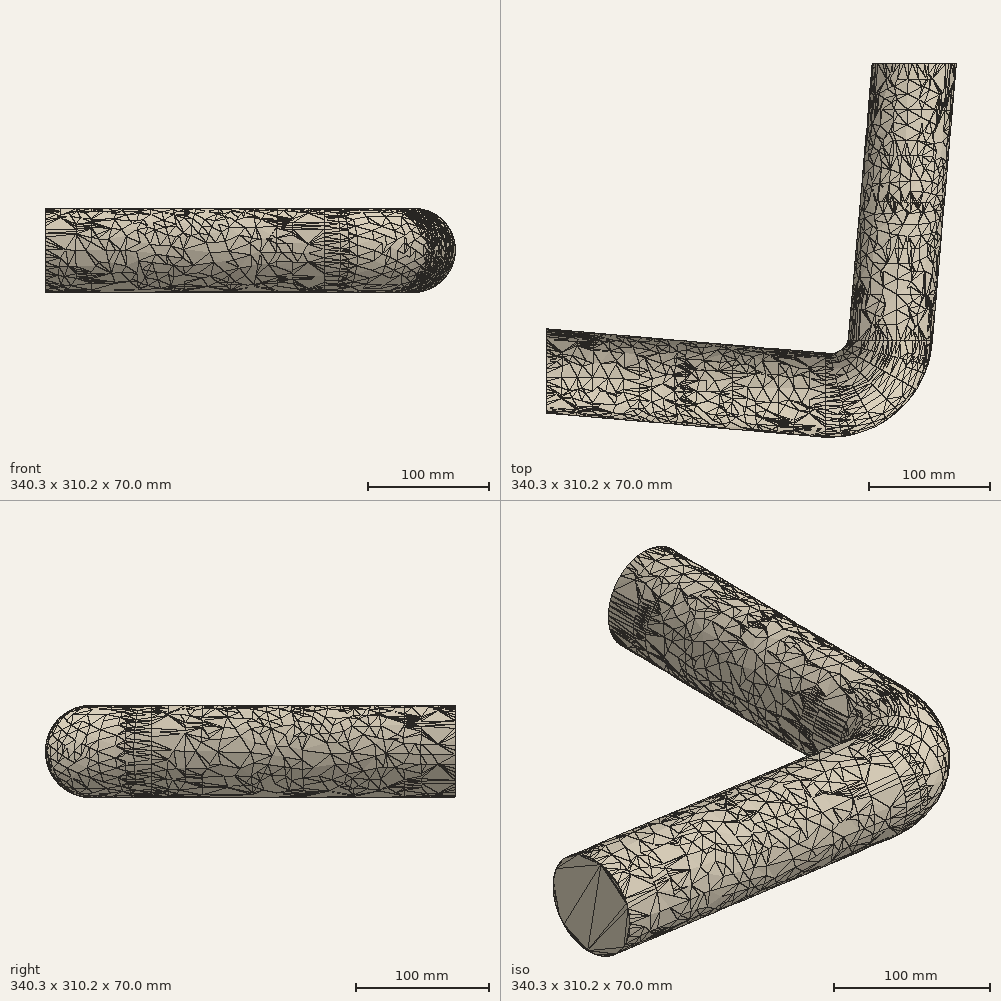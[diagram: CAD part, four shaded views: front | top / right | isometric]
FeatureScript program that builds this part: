
annotation { "Feature Type Name" : "Feature", "Feature Type Description" : "" }
export const myFeature = defineFeature(function(context is Context, id is Id, definition is map)
    precondition{}
    {
        {
            var Q0;
            Q0=qCreatedBy(makeId("Front.planeOp"),FACE);
            var sketch = newSketch(context, id + "F0", { "sketchPlane" : qUnion([Q0])});
            skCircle(sketch, "E0", {"center": v(0, 0) * mm, "radius": 35 * mm});
            skSolve(sketch);
        }
        {
            var Q0;
            Q0=qCreatedBy(makeId("Top.planeOp"),FACE);
            var sketch = newSketch(context, id + "F1", { "sketchPlane" : qUnion([Q0])});
            skLineSegment(sketch, "E1", {"start": v(0, 0) * mm, "end": v(-19.93, -229.62) * mm});
            skLineSegment(sketch, "E2", {"start": v(-74.07, -275.1) * mm, "end": v(-305.32, -255.03) * mm});
            skPoint(sketch, "E3.visualSharp", {"position": v(-24.25, -279.43) * mm});
            skArc(sketch, "E3.filletArc", {"start": v(-74.07, -275.1) * mm, "mid": v(-37.58, -263.57) * mm, "end": v(-19.93, -229.62) * mm});
            skSolve(sketch);
        }
        {
            var Q0;
            Q0 = qSketchRegion(id + "F0", true);
            var Q1;
            Q1 = qConstructionFilter(qBodyType(qCreatedBy(id + "F1" ,EDGE), BodyType.WIRE), ConstructionObject.NO);
            sweep(context, id + "F2", {"profiles" : qUnion([Q0]), "path" : qUnion([Q1])});
        }
    });
